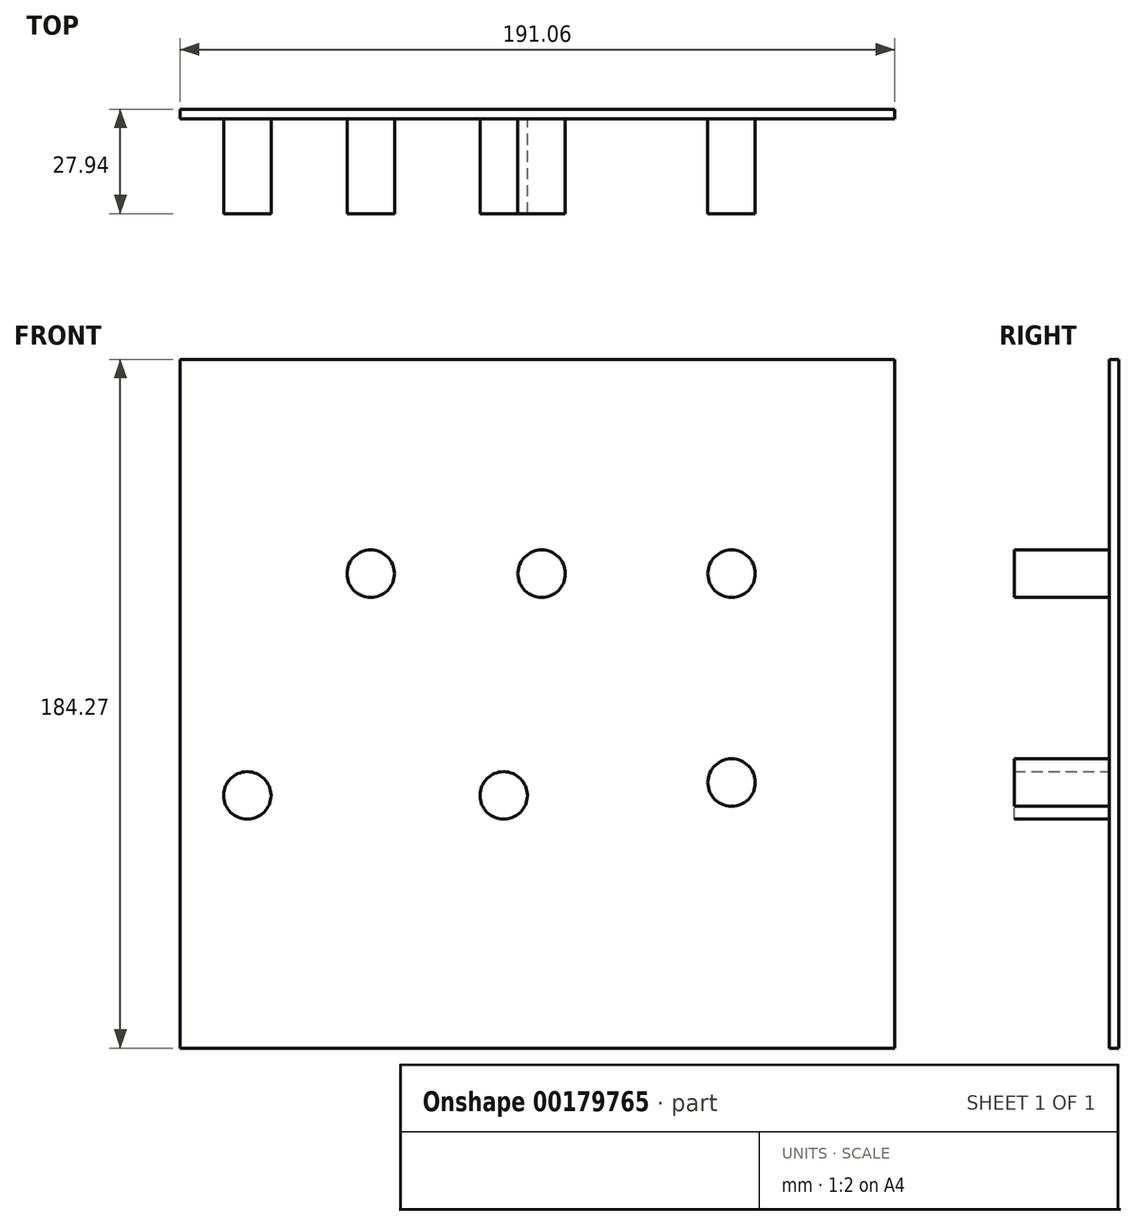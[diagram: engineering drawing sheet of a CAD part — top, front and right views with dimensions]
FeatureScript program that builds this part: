
annotation { "Feature Type Name" : "Feature", "Feature Type Description" : "" }
export const myFeature = defineFeature(function(context is Context, id is Id, definition is map)
    precondition{}
    {
        {
            var Q0;
            Q0=qCreatedBy(makeId("Front.planeOp"),FACE);
            var sketch = newSketch(context, id + "F0", { "sketchPlane" : qUnion([Q0])});
            skLineSegment(sketch, "E0.bottom", {"start": v(-96.68, 86.2) * mm, "end": v(94.38, 86.2) * mm});
            skLineSegment(sketch, "E0.top", {"start": v(-96.68, -98.07) * mm, "end": v(94.38, -98.07) * mm});
            skLineSegment(sketch, "E0.left", {"start": v(-96.68, 86.2) * mm, "end": v(-96.68, -98.07) * mm});
            skLineSegment(sketch, "E0.right", {"start": v(94.38, 86.2) * mm, "end": v(94.38, -98.07) * mm});
            skSolve(sketch);
        }
        {
            var Q0;
            Q0=makeQuery(id+"F0.imprint","IMPRINT",FACE,{"disambiguationData":[TD([[makeQuery(id+"F0.imprint","IMPRINT",EDGE,{"derivedFrom":sQuery(id+"F0.wireOp",EDGE,"E0.bottom")}),-1.0]])]});
            extrude(context, id + "F1", {"entities" : qUnion([Q0]), "depth" : 2.54 * mm});
        }
        {
            var Q0;
            Q0=makeQuery(id+"F1.opExtrude","CAP_FACE",FACE,{"disambiguationData":[OSD([sQuery(id+"F0.wireOp",EDGE,"E0.bottom"),sQuery(id+"F0.wireOp",EDGE,"E0.top"),sQuery(id+"F0.wireOp",EDGE,"E0.left"),sQuery(id+"F0.wireOp",EDGE,"E0.right")])],"isStart":false});
            var sketch = newSketch(context, id + "F2", { "sketchPlane" : qUnion([Q0])});
            skCircle(sketch, "E1", {"center": v(-45.72, 28.85) * mm, "radius": 6.35 * mm});
            skCircle(sketch, "E2", {"center": v(0, 28.85) * mm, "radius": 6.35 * mm});
            skCircle(sketch, "E3", {"center": v(50.8, 28.85) * mm, "radius": 6.35 * mm});
            skCircle(sketch, "E4", {"center": v(50.8, -27.03) * mm, "radius": 6.35 * mm});
            skCircle(sketch, "E5", {"center": v(-10.16, -30.48) * mm, "radius": 6.35 * mm});
            skCircle(sketch, "E6", {"center": v(-78.74, -30.48) * mm, "radius": 6.35 * mm});
            skSolve(sketch);
        }
        {
            var Q0;
            Q0=makeQuery(id+"F2.imprint","IMPRINT",FACE,{"disambiguationData":[TD([[makeQuery(id+"F2.imprint","IMPRINT",EDGE,{"derivedFrom":sQuery(id+"F2.wireOp",EDGE,"E1")}),1.0]])]});
            extrude(context, id + "F3", {"entities" : qUnion([Q0]), "operationType" : NewBodyOperationType.ADD, "depth" : 25.4 * mm});
        }
        {
            var Q0;
            Q0=makeQuery(id+"F2.imprint","IMPRINT",FACE,{"disambiguationData":[TD([[makeQuery(id+"F2.imprint","IMPRINT",EDGE,{"derivedFrom":sQuery(id+"F2.wireOp",EDGE,"E2")}),1.0]])]});
            var Q1;
            Q1=makeQuery(id+"F2.imprint","IMPRINT",FACE,{"disambiguationData":[TD([[makeQuery(id+"F2.imprint","IMPRINT",EDGE,{"derivedFrom":sQuery(id+"F2.wireOp",EDGE,"E3")}),1.0]])]});
            extrude(context, id + "F4", {"entities" : qUnion([Q0, Q1]), "operationType" : NewBodyOperationType.ADD, "depth" : 25.4 * mm});
        }
        {
            var Q0;
            Q0=makeQuery(id+"F2.imprint","IMPRINT",FACE,{"disambiguationData":[TD([[makeQuery(id+"F2.imprint","IMPRINT",EDGE,{"derivedFrom":sQuery(id+"F2.wireOp",EDGE,"E6")}),1.0]])]});
            extrude(context, id + "F5", {"entities" : qUnion([Q0]), "operationType" : NewBodyOperationType.ADD, "depth" : 25.4 * mm});
        }
        {
            var Q0;
            Q0=makeQuery(id+"F2.imprint","IMPRINT",FACE,{"disambiguationData":[TD([[makeQuery(id+"F2.imprint","IMPRINT",EDGE,{"derivedFrom":sQuery(id+"F2.wireOp",EDGE,"E4")}),1.0]])]});
            extrude(context, id + "F6", {"entities" : qUnion([Q0]), "operationType" : NewBodyOperationType.ADD, "depth" : 25.4 * mm});
        }
        {
            var Q0;
            Q0=makeQuery(id+"F2.imprint","IMPRINT",FACE,{"disambiguationData":[TD([[makeQuery(id+"F2.imprint","IMPRINT",EDGE,{"derivedFrom":sQuery(id+"F2.wireOp",EDGE,"E5")}),1.0]])]});
            extrude(context, id + "F7", {"entities" : qUnion([Q0]), "operationType" : NewBodyOperationType.ADD, "depth" : 25.4 * mm});
        }
    });
